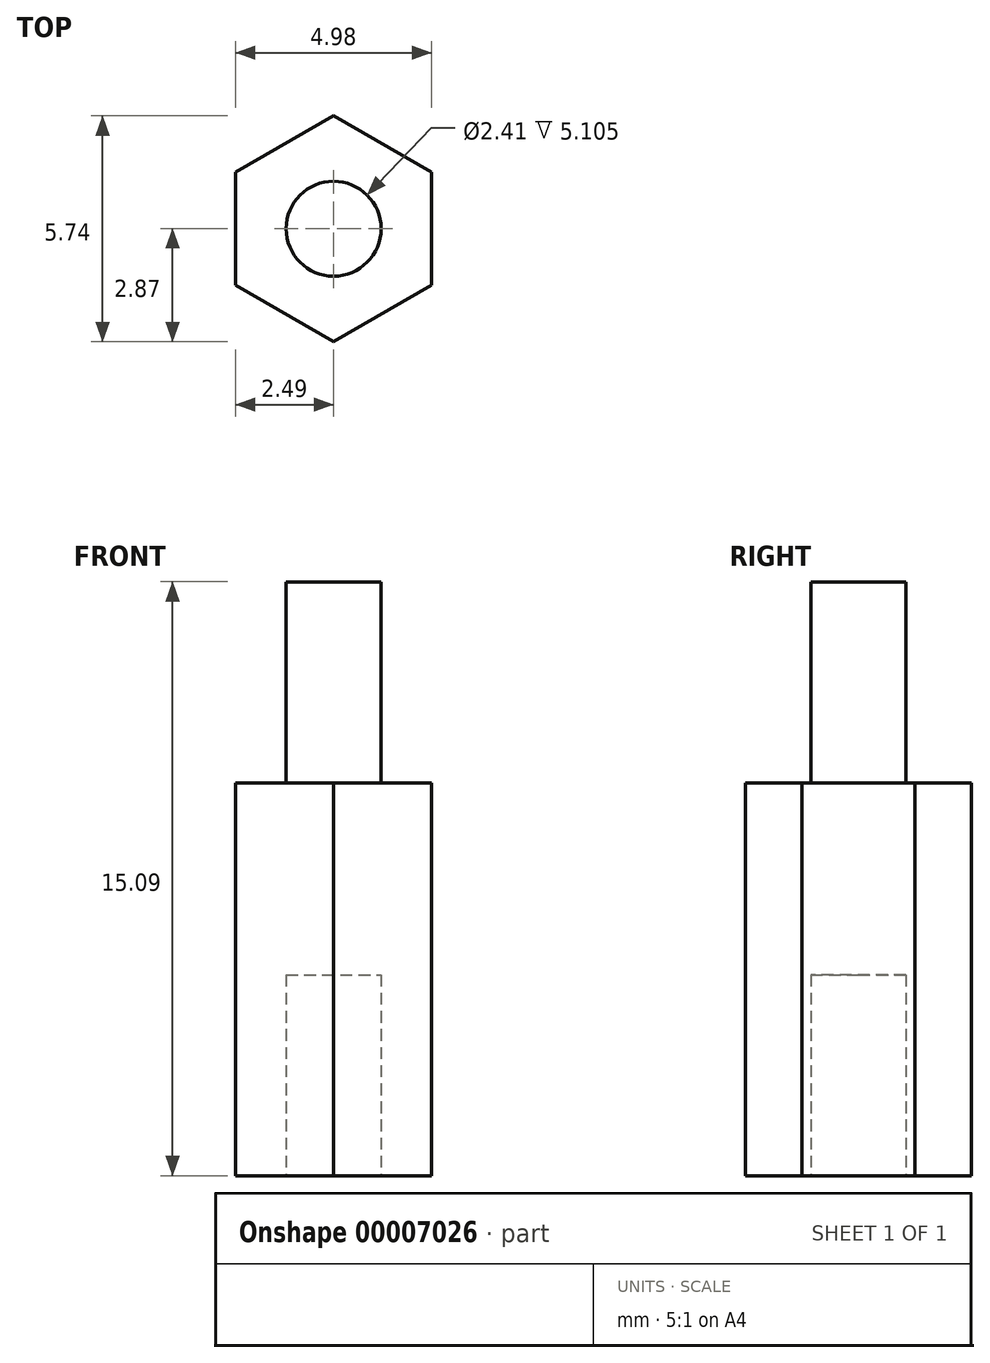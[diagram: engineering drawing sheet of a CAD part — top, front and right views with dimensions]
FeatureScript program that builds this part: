
annotation { "Feature Type Name" : "Feature", "Feature Type Description" : "" }
export const myFeature = defineFeature(function(context is Context, id is Id, definition is map)
    precondition{}
    {
        {
            var Q0;
            Q0=qCreatedBy(makeId("Top.planeOp"),FACE);
            var sketch = newSketch(context, id + "F0", { "sketchPlane" : qUnion([Q0])});
            skCircle(sketch, "E0.cCircle", {"center": v(0, 0) * mm, "radius": 2.49 * mm, "construction": true});
            skLineSegment(sketch, "E0.0", {"start": v(2.49, 1.44) * mm, "end": v(2.49, -1.44) * mm});
            skLineSegment(sketch, "E0.1", {"start": v(2.49, -1.44) * mm, "end": v(0, -2.87) * mm});
            skLineSegment(sketch, "E0.2", {"start": v(0, -2.87) * mm, "end": v(-2.49, -1.44) * mm});
            skLineSegment(sketch, "E0.3", {"start": v(-2.49, -1.44) * mm, "end": v(-2.49, 1.44) * mm});
            skLineSegment(sketch, "E0.4", {"start": v(-2.49, 1.44) * mm, "end": v(0, 2.87) * mm});
            skLineSegment(sketch, "E0.5", {"start": v(0, 2.87) * mm, "end": v(2.49, 1.44) * mm});
            skPoint(sketch, "E0.0.midPoint", {"position": v(2.49, 0) * mm});
            skCircle(sketch, "E1", {"center": v(0, 0) * mm, "radius": 1.2 * mm});
            skSolve(sketch);
        }
        {
            var Q0;
            Q0=makeQuery(id+"F0.imprint","IMPRINT",FACE,{"disambiguationData":[TD([[makeQuery(id+"F0.imprint","IMPRINT",EDGE,{"derivedFrom":sQuery(id+"F0.wireOp",EDGE,"E0.0")}),-1.0]])]});
            extrude(context, id + "F1", {"entities" : qUnion([Q0]), "depth" : 9.98 * mm});
        }
        {
            var Q0;
            Q0=makeQuery(id+"F0.imprint","IMPRINT",FACE,{"disambiguationData":[TD([[makeQuery(id+"F0.imprint","IMPRINT",EDGE,{"derivedFrom":sQuery(id+"F0.wireOp",EDGE,"E1")}),1.0]])]});
            extrude(context, id + "F2", {"entities" : qUnion([Q0]), "operationType" : NewBodyOperationType.ADD, "depth" : 15.1 * mm});
        }
        {
            var Q0;
            {var subQ0=sQuery(id+"F0.wireOp",EDGE,"E1");Q0=makeQuery(id+"F2.boolean.opBoolean","MERGE",FACE,{"derivedFrom":[makeQuery(id+"F1.opExtrude","CAP_FACE",FACE,{"disambiguationData":[OSD([sQuery(id+"F0.wireOp",EDGE,"E0.0"),sQuery(id+"F0.wireOp",EDGE,"E0.1"),sQuery(id+"F0.wireOp",EDGE,"E0.2"),sQuery(id+"F0.wireOp",EDGE,"E0.3"),sQuery(id+"F0.wireOp",EDGE,"E0.4"),sQuery(id+"F0.wireOp",EDGE,"E0.5"),subQ0])],"isStart":true}),makeQuery(id+"F2.opExtrude","CAP_FACE",FACE,{"disambiguationData":[OSD([subQ0])],"isStart":true})]});}
            var sketch = newSketch(context, id + "F3", { "sketchPlane" : qUnion([Q0])});
            skCircle(sketch, "E2", {"center": v(0, 0) * mm, "radius": 1.2 * mm});
            skSolve(sketch);
        }
        {
            var Q0;
            Q0=makeQuery(id+"F3.imprint","IMPRINT",FACE,{"disambiguationData":[TD([[makeQuery(id+"F3.imprint","IMPRINT",EDGE,{"derivedFrom":sQuery(id+"F3.wireOp",EDGE,"E2")}),1.0]])]});
            extrude(context, id + "F4", {"entities" : qUnion([Q0]), "operationType" : NewBodyOperationType.REMOVE, "oppositeDirection" : true, "depth" : 5.1 * mm});
        }
    });
